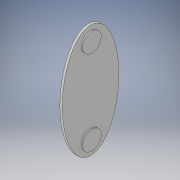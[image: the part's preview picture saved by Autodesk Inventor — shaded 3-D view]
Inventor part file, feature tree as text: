
AUTODESK INVENTOR PART (.ipt)
format: ipt  version: 2017 (Build 210142000, 142)  size: 109,568 bytes
history: native  units: in
note: dims shown in document units (in); Inventor stores cm internally (conversion verified against a paired STEP export)
features: extrude x2, sketch x2
ambient origin geometry x8: Origin, YZ Plane, XZ Plane, XY Plane, X Axis, Y Axis, Z Axis, Center Point
bodies: Solid1 (feature_tree)
feature tree (4):
  extrude  "Extrusion1"  Depth=3.0in
  extrude  "Extrusion2"  Depth=0.0625in
  sketch  "Sketch1"  dims[d0=1.5in d1=3.0in]
  sketch  "Sketch2"  dims[d2=0.125in d3=0.0in d4=2.25in d5=2.25in d6=1.002in d7=1.002in d8=0.0625in d9=0.0in]
